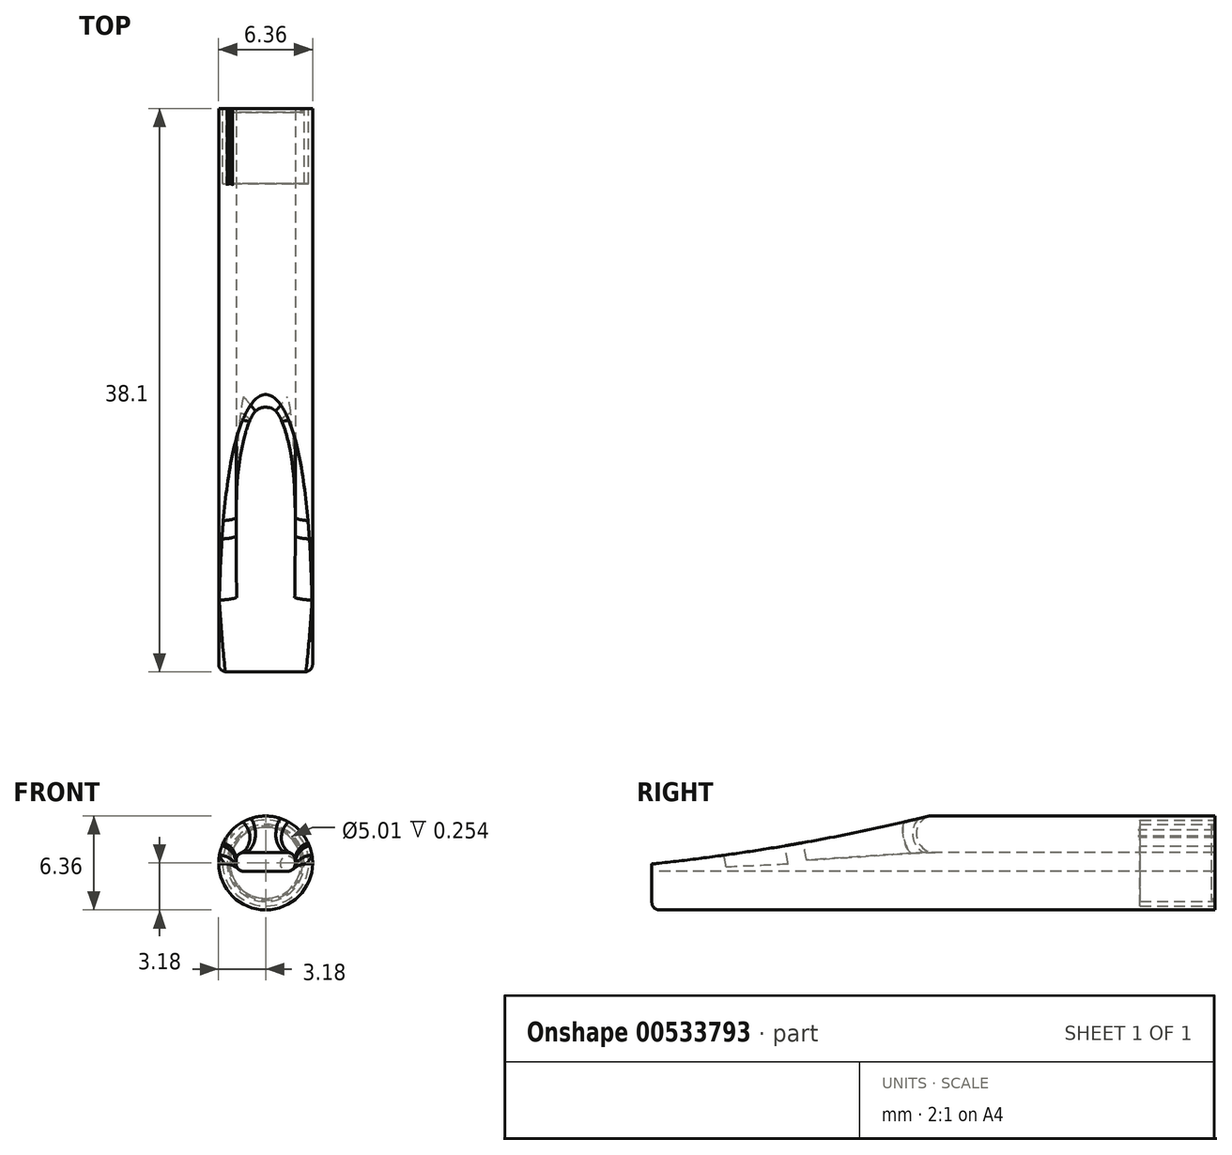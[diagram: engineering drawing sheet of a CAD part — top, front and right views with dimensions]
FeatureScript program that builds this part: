
annotation { "Feature Type Name" : "Feature", "Feature Type Description" : "" }
export const myFeature = defineFeature(function(context is Context, id is Id, definition is map)
    precondition{}
    {
        {
            var Q0;
            Q0=qCreatedBy(makeId("Front.planeOp"),FACE);
            var sketch = newSketch(context, id + "F0", { "sketchPlane" : qUnion([Q0])});
            skCircle(sketch, "E0", {"center": v(0, 0) * mm, "radius": 3.17 * mm});
            skSolve(sketch);
        }
        {
            var Q0;
            Q0=makeQuery(id+"F0.imprint","IMPRINT",FACE,{"disambiguationData":[TD([[makeQuery(id+"F0.imprint","IMPRINT",EDGE,{"derivedFrom":sQuery(id+"F0.wireOp",EDGE,"E0")}),1.0]])]});
            extrude(context, id + "F1", {"entities" : qUnion([Q0]), "depth" : 38.1 * mm, "offsetDistance" : 25.4 * mm});
        }
        {
            var Q0;
            Q0=qCreatedBy(makeId("Right.planeOp"),FACE);
            var sketch = newSketch(context, id + "F2", { "sketchPlane" : qUnion([Q0])});
            skFitSpline(sketch, "E1", {"points": [v(-61.4, 0) * mm, v(-28.65, 1.24) * mm, v(2.6, 11.13) * mm, v(-33.26, 5.74) * mm, v(-61.4, 0) * mm]});
            skSolve(sketch);
        }
        {
            var Q0;
            Q0=qSketchRegion(id+"F2",true);
            extrude(context, id + "F3", {"entities" : qUnion([Q0]), "operationType" : NewBodyOperationType.REMOVE, "endBound" : BoundingType.SYMMETRIC, "oppositeDirection" : true, "depth" : 25.4 * mm, "offsetDistance" : 25.4 * mm});
        }
        {
            var Q0;
            Q0=qCreatedBy(makeId("Front.planeOp"),FACE);
            var sketch = newSketch(context, id + "F4", { "sketchPlane" : qUnion([Q0])});
            skLineSegment(sketch, "E2", {"start": v(0, 4.82) * mm, "end": v(0, -9.2) * mm, "construction": true});
            skLineSegment(sketch, "E3.bottom", {"start": v(0, -0.56) * mm, "end": v(2, -0.56) * mm});
            skLineSegment(sketch, "E3.top", {"start": v(0, 0.7) * mm, "end": v(2, 0.7) * mm});
            skLineSegment(sketch, "E3.left", {"start": v(0, -0.56) * mm, "end": v(0, 0.7) * mm});
            skLineSegment(sketch, "E3.right", {"start": v(2, -0.56) * mm, "end": v(2, 0.7) * mm});
            skLineSegment(sketch, "E4.MirrorCS", {"start": v(0, 0.7) * mm, "end": v(-2, 0.7) * mm});
            skLineSegment(sketch, "E5.MirrorCS", {"start": v(-2, -0.56) * mm, "end": v(-2, 0.7) * mm});
            skLineSegment(sketch, "E6.MirrorCS", {"start": v(0, -0.56) * mm, "end": v(-2, -0.56) * mm});
            skSolve(sketch);
        }
        {
            var Q0;
            Q0=qSketchRegion(id+"F4",true);
            extrude(context, id + "F5", {"entities" : qUnion([Q0]), "operationType" : NewBodyOperationType.REMOVE, "endBound" : BoundingType.SYMMETRIC, "oppositeDirection" : true, "depth" : 76.2 * mm, "offsetDistance" : 25.4 * mm});
        }
        {
            var Q0;
            Q0=makeQuery(id+"F5.boolean.opBoolean","COPY",EDGE,{"derivedFrom":makeQuery(id+"F5.opExtrude","SWEPT_EDGE",EDGE,{"disambiguationData":[OSD([sQuery(id+"F4.wireOp",EDGE,"E5.MirrorCS"),sQuery(id+"F4.wireOp",EDGE,"E6.MirrorCS")])]})});
            var Q1;
            Q1=makeQuery(id+"F5.boolean.opBoolean","COPY",EDGE,{"derivedFrom":makeQuery(id+"F5.opExtrude","SWEPT_EDGE",EDGE,{"disambiguationData":[OSD([sQuery(id+"F4.wireOp",EDGE,"E3.bottom"),sQuery(id+"F4.wireOp",EDGE,"E3.right")])]})});
            var Q2;
            Q2=makeQuery(id+"F5.boolean.opBoolean","COPY",EDGE,{"derivedFrom":makeQuery(id+"F5.opExtrude","SWEPT_EDGE",EDGE,{"disambiguationData":[OSD([sQuery(id+"F4.wireOp",EDGE,"E3.top"),sQuery(id+"F4.wireOp",EDGE,"E3.right")])]})});
            var Q3;
            Q3=makeQuery(id+"F5.boolean.opBoolean","COPY",EDGE,{"derivedFrom":makeQuery(id+"F5.opExtrude","SWEPT_EDGE",EDGE,{"disambiguationData":[OSD([sQuery(id+"F4.wireOp",EDGE,"E4.MirrorCS"),sQuery(id+"F4.wireOp",EDGE,"E5.MirrorCS")])]})});
            fillet(context, id + "F6", {"entities" : qUnion([Q0, Q1, Q2, Q3]), "radius" : 0.5 * mm, "tangentPropagation" : true, "allowEdgeOverflow" : false});
        }
        {
            var Q0;
            Q0=makeQuery(id+"F1.opExtrude","CAP_EDGE",EDGE,{"disambiguationData":[OSD([sQuery(id+"F0.wireOp",EDGE,"E0")])],"isStart":false});
            fillet(context, id + "F7", {"entities" : qUnion([Q0]), "radius" : 0.5 * mm, "tangentPropagation" : true, "allowEdgeOverflow" : false});
        }
        {
            var Q0;
            Q0=makeQuery(id+"F5.boolean.opBoolean","INTERSECT",EDGE,{"derivedFrom":[makeQuery(id+"F3.boolean.opBoolean","COPY",FACE,{"derivedFrom":makeQuery(id+"F3.opExtrude","SWEPT_FACE",FACE,{"disambiguationData":[OSD([sQuery(id+"F2.wireOp",EDGE,"E1")])]})}),makeQuery(id+"F5.opExtrude","SWEPT_FACE",FACE,{"disambiguationData":[OSD([sQuery(id+"F4.wireOp",EDGE,"E3.top"),sQuery(id+"F4.wireOp",EDGE,"E4.MirrorCS")])]})]});
            fillet(context, id + "F8", {"entities" : qUnion([Q0]), "radius" : 1.27 * mm, "tangentPropagation" : true, "allowEdgeOverflow" : false});
        }
        {
            var Q0;
            Q0=makeQuery(id+"F1.opExtrude","CAP_FACE",FACE,{"disambiguationData":[OSD([sQuery(id+"F0.wireOp",EDGE,"E0")])],"isStart":true});
            var sketch = newSketch(context, id + "F9", { "sketchPlane" : qUnion([Q0])});
            skCircle(sketch, "E7", {"center": v(0, 0) * mm, "radius": 2.91 * mm});
            skCircle(sketch, "E8", {"center": v(0, 0) * mm, "radius": 2.6 * mm});
            skSolve(sketch);
        }
        {
            var Q0;
            Q0=qSketchRegion(id+"F9",true);
            extrude(context, id + "F10", {"entities" : qUnion([Q0]), "operationType" : NewBodyOperationType.REMOVE, "oppositeDirection" : true, "depth" : 5.08 * mm, "offsetDistance" : 25.4 * mm});
        }
        {
            var Q0;
            {var subQ0=sQuery(id+"F0.wireOp",EDGE,"E0");Q0=makeQuery(id+"F10.boolean.opBoolean","SPLIT",FACE,{"disambiguationData":[TD([makeQuery(id+"F1.opExtrude","SWEPT_FACE",FACE,{"disambiguationData":[OSD([subQ0])]})])],"derivedFrom":makeQuery(id+"F1.opExtrude","CAP_FACE",FACE,{"disambiguationData":[OSD([subQ0])],"isStart":true})});}
            var sketch = newSketch(context, id + "F11", { "sketchPlane" : qUnion([Q0])});
            skFitSpline(sketch, "E9", {"points": [v(2.5, 2.3) * mm, v(2.69, 0.59) * mm, v(2.44, 1.35) * mm, v(2.2, 2.91) * mm, v(2.5, 2.3) * mm]});
            skSolve(sketch);
        }
        {
            var Q0;
            Q0=qSketchRegion(id+"F11",true);
            extrude(context, id + "F12", {"entities" : qUnion([Q0]), "operationType" : NewBodyOperationType.REMOVE, "oppositeDirection" : true, "depth" : 5.08 * mm, "offsetDistance" : 25.4 * mm});
        }
        {
            var Q0;
            Q0=makeQuery(id+"F12.boolean.opBoolean","INTERSECT",EDGE,{"derivedFrom":[makeQuery(id+"F1.opExtrude","SWEPT_FACE",FACE,{"disambiguationData":[OSD([sQuery(id+"F0.wireOp",EDGE,"E0")])]}),makeQuery(id+"F12.opExtrude","CAP_FACE",FACE,{"disambiguationData":[OSD([sQuery(id+"F11.wireOp",EDGE,"E9")])],"isStart":false})]});
            fillet(context, id + "F13", {"entities" : qUnion([Q0]), "radius" : 0.13 * mm, "tangentPropagation" : true, "allowEdgeOverflow" : false});
        }
        {
            var Q0;
            {var subQ1=sQuery(id+"F4.wireOp",EDGE,"E3.right");Q0=makeQuery(id+"F10.boolean.opBoolean","SPLIT",FACE,{"disambiguationData":[TD([makeQuery(id+"F5.boolean.opBoolean","COPY",FACE,{"derivedFrom":makeQuery(id+"F5.opExtrude","SWEPT_FACE",FACE,{"disambiguationData":[OSD([subQ1])]})})])],"derivedFrom":makeQuery(id+"F1.opExtrude","CAP_FACE",FACE,{"disambiguationData":[OSD([sQuery(id+"F0.wireOp",EDGE,"E0")])],"isStart":true})});}
            var sketch = newSketch(context, id + "F14", { "sketchPlane" : qUnion([Q0])});
            skCircle(sketch, "E10", {"center": v(0, 0) * mm, "radius": 2.5 * mm});
            skCircle(sketch, "E11", {"center": v(0, 0) * mm, "radius": 2.4 * mm});
            skSolve(sketch);
        }
        {
            var Q0;
            Q0=qSketchRegion(id+"F14",true);
            extrude(context, id + "F15", {"entities" : qUnion([Q0]), "operationType" : NewBodyOperationType.REMOVE, "oppositeDirection" : true, "depth" : 0.25 * mm, "offsetDistance" : 25.4 * mm});
        }
        {
            var Q0;
            {var subQ2=sQuery(id+"F4.wireOp",EDGE,"E3.right");var subQ3=makeQuery(id+"F5.boolean.opBoolean","COPY",FACE,{"derivedFrom":makeQuery(id+"F5.opExtrude","SWEPT_FACE",FACE,{"disambiguationData":[OSD([subQ2])]})});Q0=makeQuery(id+"F15.boolean.opBoolean","SPLIT",FACE,{"disambiguationData":[TD([subQ3])],"derivedFrom":makeQuery(id+"F10.boolean.opBoolean","SPLIT",FACE,{"disambiguationData":[TD([subQ3])],"derivedFrom":makeQuery(id+"F1.opExtrude","CAP_FACE",FACE,{"disambiguationData":[OSD([sQuery(id+"F0.wireOp",EDGE,"E0")])],"isStart":true})})});}
            fillet(context, id + "F16", {"entities" : qUnion([Q0]), "radius" : 0.05 * mm, "tangentPropagation" : true, "allowEdgeOverflow" : false});
        }
    });
